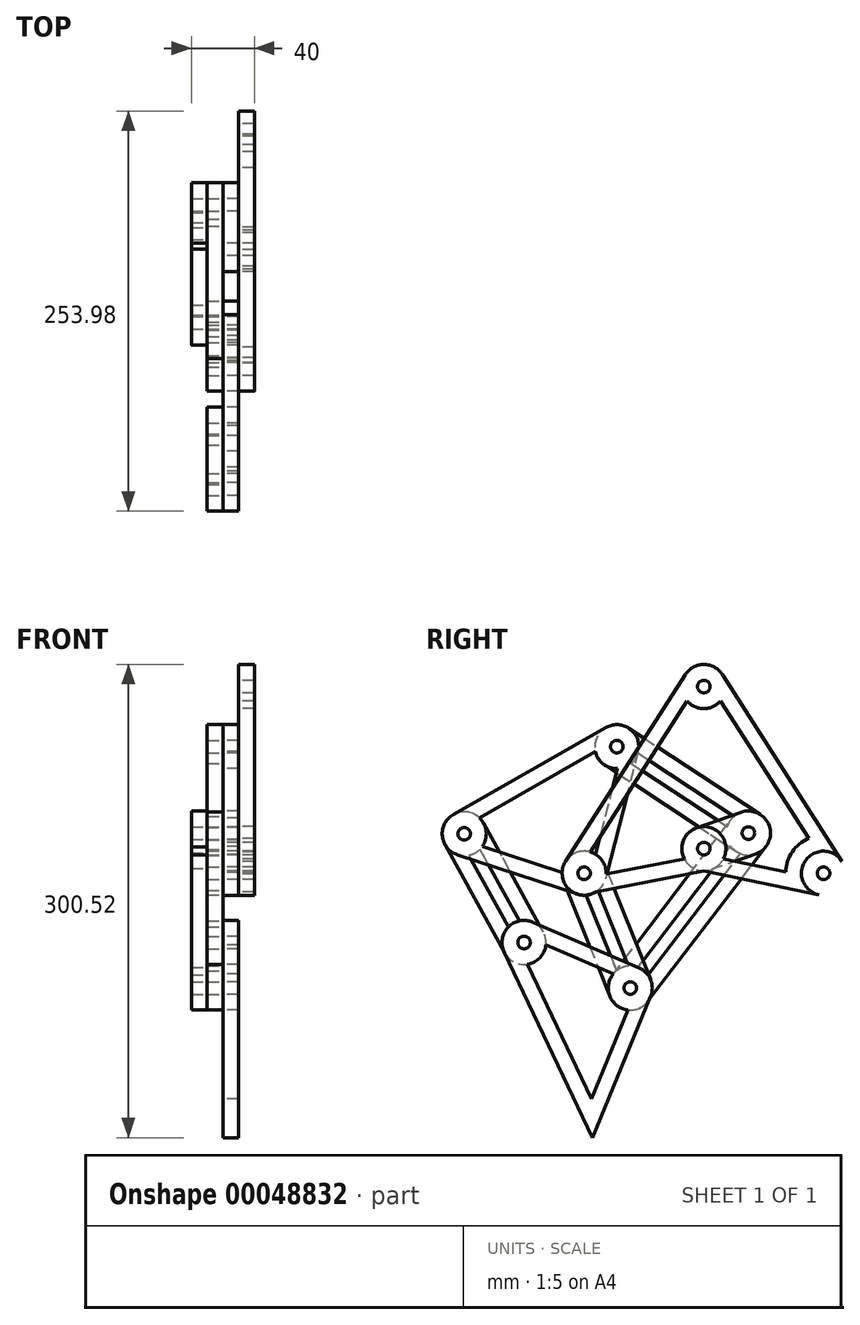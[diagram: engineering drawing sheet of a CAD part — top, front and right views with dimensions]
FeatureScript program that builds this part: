
annotation { "Feature Type Name" : "Feature", "Feature Type Description" : "" }
export const myFeature = defineFeature(function(context is Context, id is Id, definition is map)
    precondition{}
    {
        {
            assignVariable(context, id + "F0", {"name" : "WALL", "anyValue" : 10});
        }
        {
            var Q0;
            Q0=qCreatedBy(makeId("Right.planeOp"),FACE);
            var sketch = newSketch(context, id + "F1", { "sketchPlane" : qUnion([Q0])});
            skCircle(sketch, "E0", {"center": v(0, 0) * mm, "radius": 5.71 * mm});
            skLineSegment(sketch, "E1", {"start": v(0, 0) * mm, "end": v(28.32, 9.9) * mm});
            skLineSegment(sketch, "E2", {"start": v(28.32, 9.9) * mm, "end": v(-55.28, 64.77) * mm});
            skLineSegment(sketch, "E3", {"start": v(-55.28, 64.77) * mm, "end": v(-76, -15.6) * mm});
            skLineSegment(sketch, "E4", {"start": v(-76, -15.6) * mm, "end": v(-46.74, -88.55) * mm});
            skLineSegment(sketch, "E5", {"start": v(-46.74, -88.55) * mm, "end": v(28.32, 9.9) * mm});
            skLineSegment(sketch, "E6", {"start": v(-76, -15.6) * mm, "end": v(-152.2, 9.43) * mm});
            skLineSegment(sketch, "E7", {"start": v(-152.2, 9.43) * mm, "end": v(-55.28, 64.77) * mm});
            skLineSegment(sketch, "E8", {"start": v(-46.74, -88.55) * mm, "end": v(-114.19, -59.6) * mm});
            skLineSegment(sketch, "E9", {"start": v(-114.19, -59.6) * mm, "end": v(-152.2, 9.43) * mm});
            skLineSegment(sketch, "E10", {"start": v(-114.19, -59.6) * mm, "end": v(-70.68, -183.58) * mm});
            skLineSegment(sketch, "E11", {"start": v(-70.68, -183.58) * mm, "end": v(-46.74, -88.55) * mm});
            skCircle(sketch, "E12", {"center": v(-76, -15.6) * mm, "radius": 83 * mm, "construction": true});
            skLineSegment(sketch, "E13", {"start": v(0, 0) * mm, "end": v(-22.73, 19.58) * mm});
            skCircle(sketch, "E14", {"center": v(-55.28, 64.77) * mm, "radius": 14 * mm, "construction": true});
            skCircle(sketch, "E15", {"center": v(28.32, 9.9) * mm, "radius": 14 * mm, "construction": true});
            skCircle(sketch, "E16", {"center": v(0, 0) * mm, "radius": 44 * mm, "construction": true});
            skLineSegment(sketch, "E17", {"start": v(0, 0) * mm, "end": v(0, 67.08) * mm, "construction": true});
            skSolve(sketch);
        }
        {
            var Q0;
            Q0=qCreatedBy(makeId("Right.planeOp"),FACE);
            var sketch = newSketch(context, id + "F2", { "sketchPlane" : qUnion([Q0])});
            skLineSegment(sketch, "E18.rect.bottom", {"start": v(-228.6, 228.6) * mm, "end": v(228.6, 228.6) * mm, "construction": true});
            skLineSegment(sketch, "E18.rect.top", {"start": v(-228.6, -228.6) * mm, "end": v(228.6, -228.6) * mm, "construction": true});
            skLineSegment(sketch, "E18.rect.left", {"start": v(-228.6, 228.6) * mm, "end": v(-228.6, -228.6) * mm, "construction": true});
            skLineSegment(sketch, "E18.rect.right", {"start": v(228.6, 228.6) * mm, "end": v(228.6, -228.6) * mm, "construction": true});
            skPoint(sketch, "E18.rect.middle", {"position": v(0, 0) * mm});
            skSolve(sketch);
        }
        {
            var Q0;
            Q0=qCreatedBy(makeId("Right.planeOp"),FACE);
            var sketch = newSketch(context, id + "F3", { "sketchPlane" : qUnion([Q0])});
            skCircle(sketch, "E19", {"center": v(-152.2, 9.43) * mm, "radius": 4 * mm});
            skCircle(sketch, "E20", {"center": v(-55.28, 64.77) * mm, "radius": 4 * mm});
            skCircle(sketch, "E21", {"center": v(-76, -15.6) * mm, "radius": 4 * mm});
            skCircle(sketch, "E22", {"center": v(0, 0) * mm, "radius": 4 * mm});
            skCircle(sketch, "E23", {"center": v(28.32, 9.9) * mm, "radius": 4 * mm});
            skCircle(sketch, "E24", {"center": v(-114.19, -59.6) * mm, "radius": 4 * mm});
            skCircle(sketch, "E25", {"center": v(-46.74, -88.55) * mm, "radius": 4 * mm});
            skCircle(sketch, "E26", {"center": v(-152.2, 9.43) * mm, "radius": 14 * mm});
            skCircle(sketch, "E27", {"center": v(-114.19, -59.6) * mm, "radius": 14 * mm});
            skCircle(sketch, "E28", {"center": v(-46.74, -88.55) * mm, "radius": 14 * mm});
            skCircle(sketch, "E29", {"center": v(-76, -15.6) * mm, "radius": 14 * mm});
            skCircle(sketch, "E30", {"center": v(-55.28, 64.77) * mm, "radius": 14 * mm});
            skCircle(sketch, "E31", {"center": v(28.32, 9.9) * mm, "radius": 14 * mm});
            skCircle(sketch, "E32", {"center": v(0, 0) * mm, "radius": 14 * mm});
            skCircle(sketch, "E33", {"center": v(-22.73, 19.58) * mm, "radius": 4 * mm});
            skCircle(sketch, "E34", {"center": v(-22.73, 19.58) * mm, "radius": 14 * mm});
            skLineSegment(sketch, "E35", {"start": v(-159.13, 21.6) * mm, "end": v(-62.22, 76.93) * mm});
            skLineSegment(sketch, "E36", {"start": v(-41.72, 61.28) * mm, "end": v(-62.44, -19.1) * mm});
            skLineSegment(sketch, "E37", {"start": v(-80.37, -28.9) * mm, "end": v(-156.56, -3.87) * mm});
            skLineSegment(sketch, "E38", {"start": v(-108.67, -46.73) * mm, "end": v(-41.22, -75.69) * mm});
            skLineSegment(sketch, "E39", {"start": v(-126.83, -65.61) * mm, "end": v(-70.68, -183.58) * mm});
            skLineSegment(sketch, "E40", {"start": v(-70.68, -183.58) * mm, "end": v(-33.8, -93.88) * mm});
            skLineSegment(sketch, "E41", {"start": v(4.62, -13.22) * mm, "end": v(32.94, -3.32) * mm});
            skLineSegment(sketch, "E42", {"start": v(-4.62, 13.22) * mm, "end": v(23.7, 23.11) * mm});
            skSolve(sketch);
        }
        {
            var Q0;
            Q0=qCreatedBy(makeId("Right.planeOp"),FACE);
            var sketch = newSketch(context, id + "F4", { "sketchPlane" : qUnion([Q0])});
            skCircle(sketch, "E43.0", {"center": v(-152.2, 9.43) * mm, "radius": 14 * mm});
            skCircle(sketch, "E43.1", {"center": v(-76, -15.6) * mm, "radius": 14 * mm});
            skCircle(sketch, "E43.2", {"center": v(-114.19, -59.6) * mm, "radius": 14 * mm});
            skCircle(sketch, "E43.3", {"center": v(-46.74, -88.55) * mm, "radius": 14 * mm});
            skCircle(sketch, "E43.4", {"center": v(-55.28, 64.77) * mm, "radius": 14 * mm});
            skCircle(sketch, "E43.5", {"center": v(28.32, 9.9) * mm, "radius": 14 * mm});
            skLineSegment(sketch, "E44", {"start": v(-164.46, 2.68) * mm, "end": v(-126.45, -66.35) * mm});
            skLineSegment(sketch, "E45", {"start": v(-101.92, -52.84) * mm, "end": v(-139.93, 16.19) * mm});
            skLineSegment(sketch, "E46", {"start": v(-89, -20.81) * mm, "end": v(-59.74, -93.76) * mm});
            skLineSegment(sketch, "E47", {"start": v(-63, -10.39) * mm, "end": v(-33.75, -83.34) * mm});
            skLineSegment(sketch, "E48", {"start": v(-47.6, 76.48) * mm, "end": v(36, 21.6) * mm});
            skLineSegment(sketch, "E49", {"start": v(-62.96, 53.07) * mm, "end": v(20.64, -1.8) * mm});
            skCircle(sketch, "E50.0", {"center": v(-152.2, 9.43) * mm, "radius": 4 * mm});
            skCircle(sketch, "E50.1", {"center": v(-114.19, -59.6) * mm, "radius": 4 * mm});
            skCircle(sketch, "E50.2", {"center": v(-76, -15.6) * mm, "radius": 4 * mm});
            skCircle(sketch, "E50.3", {"center": v(-46.74, -88.55) * mm, "radius": 4 * mm});
            skCircle(sketch, "E50.4", {"center": v(-55.28, 64.77) * mm, "radius": 4 * mm});
            skCircle(sketch, "E50.5", {"center": v(28.32, 9.9) * mm, "radius": 4 * mm});
            skSolve(sketch);
        }
        {
            var Q0;
            Q0=qCreatedBy(makeId("Right.planeOp"),FACE);
            var sketch = newSketch(context, id + "F5", { "sketchPlane" : qUnion([Q0])});
            skCircle(sketch, "E51.0", {"center": v(-46.74, -88.55) * mm, "radius": 4 * mm});
            skCircle(sketch, "E51.1", {"center": v(-46.74, -88.55) * mm, "radius": 14 * mm});
            skCircle(sketch, "E51.2", {"center": v(28.32, 9.9) * mm, "radius": 4 * mm});
            skCircle(sketch, "E51.3", {"center": v(28.32, 9.9) * mm, "radius": 14 * mm});
            skCircle(sketch, "E51.4", {"center": v(0, 0) * mm, "radius": 4 * mm});
            skCircle(sketch, "E51.5", {"center": v(-76, -15.6) * mm, "radius": 4 * mm});
            skCircle(sketch, "E51.6", {"center": v(-76, -15.6) * mm, "radius": 14 * mm});
            skCircle(sketch, "E51.7", {"center": v(0, 0) * mm, "radius": 14 * mm});
            skLineSegment(sketch, "E52", {"start": v(-57.87, -80.06) * mm, "end": v(17.19, 18.39) * mm});
            skLineSegment(sketch, "E53", {"start": v(-35.6, -97.04) * mm, "end": v(39.45, 1.4) * mm});
            skCircle(sketch, "E54", {"center": v(0, 102.94) * mm, "radius": 4 * mm});
            skCircle(sketch, "E55", {"center": v(0, 102.94) * mm, "radius": 14 * mm});
            skLineSegment(sketch, "E56", {"start": v(-87.79, -8.04) * mm, "end": v(-11.79, 110.5) * mm});
            skCircle(sketch, "E57.MirrorC", {"center": v(76, -15.6) * mm, "radius": 4 * mm});
            skCircle(sketch, "E58.MirrorC", {"center": v(76, -15.6) * mm, "radius": 14 * mm});
            skLineSegment(sketch, "E59", {"start": v(87.79, -8.04) * mm, "end": v(11.79, 110.5) * mm});
            skLineSegment(sketch, "E60", {"start": v(-68.65, -27.51) * mm, "end": v(0, -14.26) * mm});
            skLineSegment(sketch, "E61", {"start": v(0, -14.26) * mm, "end": v(73.18, -29.31) * mm});
            skSolve(sketch);
        }
        {
            var Q0;
            Q0=makeQuery(id+"F3.imprint","IMPRINT",FACE,{"disambiguationData":[TD([[makeQuery(id+"F3.imprint","IMPRINT",EDGE,{"derivedFrom":sQuery(id+"F3.wireOp",EDGE,"E19")}),-1.0]])]});
            var Q1;
            {var subQ3=sQuery(id+"F3.wireOp",EDGE,"E35");Q1=makeQuery(id+"F3.imprint","IMPRINT",FACE,{"disambiguationData":[TD([[makeQuery(id+"F3.imprint","IMPRINT",EDGE,{"derivedFrom":subQ3}),-1.0]])]});}
            var Q2;
            Q2=makeQuery(id+"F3.imprint","IMPRINT",FACE,{"disambiguationData":[TD([[makeQuery(id+"F3.imprint","IMPRINT",EDGE,{"derivedFrom":sQuery(id+"F3.wireOp",EDGE,"E21")}),-1.0]])]});
            var Q3;
            Q3=makeQuery(id+"F3.imprint","IMPRINT",FACE,{"disambiguationData":[TD([[makeQuery(id+"F3.imprint","IMPRINT",EDGE,{"derivedFrom":sQuery(id+"F3.wireOp",EDGE,"E20")}),-1.0]])]});
            var Q4;
            Q4=makeQuery(id+"F3.imprint","IMPRINT",FACE,{"disambiguationData":[TD([[makeQuery(id+"F3.imprint","IMPRINT",EDGE,{"derivedFrom":sQuery(id+"F3.wireOp",EDGE,"E22")}),-1.0]])]});
            var Q5;
            {var subQ0=sQuery(id+"F3.wireOp",EDGE,"E41");Q5=makeQuery(id+"F3.imprint","IMPRINT",FACE,{"disambiguationData":[TD([[makeQuery(id+"F3.imprint","IMPRINT",EDGE,{"derivedFrom":subQ0}),1.0]])]});}
            var Q6;
            Q6=makeQuery(id+"F3.imprint","IMPRINT",FACE,{"disambiguationData":[TD([[makeQuery(id+"F3.imprint","IMPRINT",EDGE,{"derivedFrom":sQuery(id+"F3.wireOp",EDGE,"E23")}),-1.0]])]});
            var Q7;
            {var subQ3=sQuery(id+"F3.wireOp",EDGE,"E38");Q7=makeQuery(id+"F3.imprint","IMPRINT",FACE,{"disambiguationData":[TD([[makeQuery(id+"F3.imprint","IMPRINT",EDGE,{"derivedFrom":subQ3}),-1.0]])]});}
            var Q8;
            Q8=makeQuery(id+"F3.imprint","IMPRINT",FACE,{"disambiguationData":[TD([[makeQuery(id+"F3.imprint","IMPRINT",EDGE,{"derivedFrom":sQuery(id+"F3.wireOp",EDGE,"E24")}),-1.0]])]});
            var Q9;
            Q9=makeQuery(id+"F3.imprint","IMPRINT",FACE,{"disambiguationData":[TD([[makeQuery(id+"F3.imprint","IMPRINT",EDGE,{"derivedFrom":sQuery(id+"F3.wireOp",EDGE,"E25")}),-1.0]])]});
            extrude(context, id + "F6", {"entities" : qUnion([Q0, Q1, Q2, Q3, Q4, Q5, Q6, Q7, Q8, Q9]), "depth" : (getVariable(context, 'WALL')) * mm});
        }
        {
            var Q0;
            Q0=makeQuery(id+"F4.imprint","IMPRINT",FACE,{"disambiguationData":[TD([[makeQuery(id+"F4.imprint","IMPRINT",EDGE,{"derivedFrom":sQuery(id+"F4.wireOp",EDGE,"E50.0")}),-1.0]])]});
            var Q1;
            {var subQ1=sQuery(id+"F4.wireOp",EDGE,"E44");Q1=makeQuery(id+"F4.imprint","IMPRINT",FACE,{"disambiguationData":[TD([[makeQuery(id+"F4.imprint","IMPRINT",EDGE,{"derivedFrom":subQ1}),1.0]])]});}
            var Q2;
            Q2=makeQuery(id+"F4.imprint","IMPRINT",FACE,{"disambiguationData":[TD([[makeQuery(id+"F4.imprint","IMPRINT",EDGE,{"derivedFrom":sQuery(id+"F4.wireOp",EDGE,"E50.1")}),-1.0]])]});
            var Q3;
            Q3=makeQuery(id+"F4.imprint","IMPRINT",FACE,{"disambiguationData":[TD([[makeQuery(id+"F4.imprint","IMPRINT",EDGE,{"derivedFrom":sQuery(id+"F4.wireOp",EDGE,"E50.2")}),-1.0]])]});
            var Q4;
            {var subQ1=sQuery(id+"F4.wireOp",EDGE,"E46");Q4=makeQuery(id+"F4.imprint","IMPRINT",FACE,{"disambiguationData":[TD([[makeQuery(id+"F4.imprint","IMPRINT",EDGE,{"derivedFrom":subQ1}),1.0]])]});}
            var Q5;
            Q5=makeQuery(id+"F4.imprint","IMPRINT",FACE,{"disambiguationData":[TD([[makeQuery(id+"F4.imprint","IMPRINT",EDGE,{"derivedFrom":sQuery(id+"F4.wireOp",EDGE,"E50.3")}),-1.0]])]});
            var Q6;
            Q6=makeQuery(id+"F4.imprint","IMPRINT",FACE,{"disambiguationData":[TD([[makeQuery(id+"F4.imprint","IMPRINT",EDGE,{"derivedFrom":sQuery(id+"F4.wireOp",EDGE,"E50.4")}),-1.0]])]});
            var Q7;
            {var subQ1=sQuery(id+"F4.wireOp",EDGE,"E48");Q7=makeQuery(id+"F4.imprint","IMPRINT",FACE,{"disambiguationData":[TD([[makeQuery(id+"F4.imprint","IMPRINT",EDGE,{"derivedFrom":subQ1}),-1.0]])]});}
            var Q8;
            Q8=makeQuery(id+"F4.imprint","IMPRINT",FACE,{"disambiguationData":[TD([[makeQuery(id+"F4.imprint","IMPRINT",EDGE,{"derivedFrom":sQuery(id+"F4.wireOp",EDGE,"E50.5")}),-1.0]])]});
            extrude(context, id + "F7", {"entities" : qUnion([Q0, Q1, Q2, Q3, Q4, Q5, Q6, Q7, Q8]), "oppositeDirection" : true, "depth" : (getVariable(context, 'WALL')) * mm});
        }
        {
            var Q0;
            Q0=makeQuery(id+"F5.imprint","IMPRINT",FACE,{"disambiguationData":[TD([[makeQuery(id+"F5.imprint","IMPRINT",EDGE,{"derivedFrom":sQuery(id+"F5.wireOp",EDGE,"E51.2")}),-1.0]])]});
            var Q1;
            {var subQ3=sQuery(id+"F5.wireOp",EDGE,"E51.3");var subQ5=sQuery(id+"F5.wireOp",EDGE,"E52");var subQ6=makeQuery(id+"F5.imprint","INTERSECT",VERTEX,{"derivedFrom":[subQ3,subQ5]});Q1=makeQuery(id+"F5.imprint","IMPRINT",FACE,{"disambiguationData":[TD([[makeQuery(id+"F5.imprint","IMPRINT",EDGE,{"disambiguationData":[TD([[subQ6,-1.0]])],"derivedFrom":subQ3}),-1.0]])]});}
            var Q2;
            {var subQ0=sQuery(id+"F5.wireOp",EDGE,"E52");var subQ1=sQuery(id+"F5.wireOp",EDGE,"E51.7");var subQ3=makeQuery(id+"F5.imprint","INTERSECT",VERTEX,{"disambiguationData":[OD(0.0)],"derivedFrom":[subQ1,subQ0]});Q2=makeQuery(id+"F5.imprint","IMPRINT",FACE,{"disambiguationData":[TD([[makeQuery(id+"F5.imprint","IMPRINT",EDGE,{"disambiguationData":[TD([[subQ3,-1.0]])],"derivedFrom":subQ1}),1.0]])]});}
            var Q3;
            {var subQ3=sQuery(id+"F5.wireOp",EDGE,"E52");var subQ5=sQuery(id+"F5.wireOp",EDGE,"E51.1");var subQ7=makeQuery(id+"F5.imprint","INTERSECT",VERTEX,{"derivedFrom":[subQ5,subQ3]});Q3=makeQuery(id+"F5.imprint","IMPRINT",FACE,{"disambiguationData":[TD([[makeQuery(id+"F5.imprint","IMPRINT",EDGE,{"disambiguationData":[TD([[subQ7,1.0]])],"derivedFrom":subQ5}),-1.0]])]});}
            var Q4;
            Q4=makeQuery(id+"F5.imprint","IMPRINT",FACE,{"disambiguationData":[TD([[makeQuery(id+"F5.imprint","IMPRINT",EDGE,{"derivedFrom":sQuery(id+"F5.wireOp",EDGE,"E51.0")}),-1.0]])]});
            extrude(context, id + "F8", {"entities" : qUnion([Q0, Q1, Q2, Q3, Q4]), "oppositeDirection" : true, "depth" : (getVariable(context, 'WALL') * 2) * mm, "hasSecondDirection" : true, "secondDirectionOppositeDirection" : true, "secondDirectionDepth" : (getVariable(context, 'WALL')) * mm});
        }
        {
            var Q0;
            Q0=makeQuery(id+"F5.imprint","IMPRINT",FACE,{"disambiguationData":[TD([[makeQuery(id+"F5.imprint","IMPRINT",EDGE,{"derivedFrom":sQuery(id+"F5.wireOp",EDGE,"E51.5")}),-1.0]])]});
            var Q1;
            {var subQ15=sQuery(id+"F5.wireOp",EDGE,"E56");Q1=makeQuery(id+"F5.imprint","IMPRINT",FACE,{"disambiguationData":[TD([[makeQuery(id+"F5.imprint","IMPRINT",EDGE,{"derivedFrom":subQ15}),-1.0]])]});}
            var Q2;
            Q2=makeQuery(id+"F5.imprint","IMPRINT",FACE,{"disambiguationData":[TD([[makeQuery(id+"F5.imprint","IMPRINT",EDGE,{"derivedFrom":sQuery(id+"F5.wireOp",EDGE,"E54")}),-1.0]])]});
            var Q3;
            Q3=makeQuery(id+"F5.imprint","IMPRINT",FACE,{"disambiguationData":[TD([[makeQuery(id+"F5.imprint","IMPRINT",EDGE,{"derivedFrom":sQuery(id+"F5.wireOp",EDGE,"E51.4")}),-1.0]])]});
            var Q4;
            {var subQ0=sQuery(id+"F5.wireOp",EDGE,"E52");var subQ1=sQuery(id+"F5.wireOp",EDGE,"E51.7");var subQ3=makeQuery(id+"F5.imprint","INTERSECT",VERTEX,{"disambiguationData":[OD(0.0)],"derivedFrom":[subQ1,subQ0]});Q4=makeQuery(id+"F5.imprint","IMPRINT",FACE,{"disambiguationData":[TD([[makeQuery(id+"F5.imprint","IMPRINT",EDGE,{"disambiguationData":[TD([[subQ3,-1.0]])],"derivedFrom":subQ1}),1.0]])]});}
            var Q5;
            {var subQ3=sQuery(id+"F5.wireOp",EDGE,"E51.3");var subQ5=sQuery(id+"F5.wireOp",EDGE,"E52");var subQ6=makeQuery(id+"F5.imprint","INTERSECT",VERTEX,{"derivedFrom":[subQ3,subQ5]});Q5=makeQuery(id+"F5.imprint","IMPRINT",FACE,{"disambiguationData":[TD([[makeQuery(id+"F5.imprint","IMPRINT",EDGE,{"disambiguationData":[TD([[subQ6,-1.0]])],"derivedFrom":subQ3}),-1.0]])]});}
            var Q6;
            Q6=makeQuery(id+"F5.imprint","IMPRINT",FACE,{"disambiguationData":[TD([[makeQuery(id+"F5.imprint","IMPRINT",EDGE,{"derivedFrom":sQuery(id+"F5.wireOp",EDGE,"E51.2")}),-1.0]])]});
            var Q7;
            Q7=makeQuery(id+"F5.imprint","IMPRINT",FACE,{"disambiguationData":[TD([[makeQuery(id+"F5.imprint","IMPRINT",EDGE,{"derivedFrom":sQuery(id+"F5.wireOp",EDGE,"E51.2")}),1.0]])]});
            var Q8;
            Q8=makeQuery(id+"F5.imprint","IMPRINT",FACE,{"disambiguationData":[TD([[makeQuery(id+"F5.imprint","IMPRINT",EDGE,{"derivedFrom":sQuery(id+"F5.wireOp",EDGE,"E57.MirrorC")}),1.0]])]});
            extrude(context, id + "F9", {"entities" : qUnion([Q0, Q1, Q2, Q3, Q4, Q5, Q6, Q7, Q8]), "depth" : (getVariable(context, 'WALL') * 2) * mm, "hasSecondDirection" : true, "secondDirectionOppositeDirection" : false, "secondDirectionDepth" : (getVariable(context, 'WALL') * 1) * mm});
        }
        {
            var Q0;
            Q0=makeQuery(id+"F6.opExtrude","CAP_FACE",FACE,{"disambiguationData":[OSD([sQuery(id+"F3.wireOp",EDGE,"E19"),sQuery(id+"F3.wireOp",EDGE,"E20"),sQuery(id+"F3.wireOp",EDGE,"E21"),sQuery(id+"F3.wireOp",EDGE,"E26"),sQuery(id+"F3.wireOp",EDGE,"E29"),sQuery(id+"F3.wireOp",EDGE,"E30"),sQuery(id+"F3.wireOp",EDGE,"E35"),sQuery(id+"F3.wireOp",EDGE,"E36"),sQuery(id+"F3.wireOp",EDGE,"E37")])],"isStart":false});
            var Q1;
            Q1=makeQuery(id+"F6.opExtrude","CAP_FACE",FACE,{"disambiguationData":[OSD([sQuery(id+"F3.wireOp",EDGE,"E19"),sQuery(id+"F3.wireOp",EDGE,"E20"),sQuery(id+"F3.wireOp",EDGE,"E21"),sQuery(id+"F3.wireOp",EDGE,"E26"),sQuery(id+"F3.wireOp",EDGE,"E29"),sQuery(id+"F3.wireOp",EDGE,"E30"),sQuery(id+"F3.wireOp",EDGE,"E35"),sQuery(id+"F3.wireOp",EDGE,"E36"),sQuery(id+"F3.wireOp",EDGE,"E37")])],"isStart":true});
            var Q2;
            Q2=makeQuery(id+"F6.opExtrude","CAP_FACE",FACE,{"disambiguationData":[OSD([sQuery(id+"F3.wireOp",EDGE,"E24"),sQuery(id+"F3.wireOp",EDGE,"E25"),sQuery(id+"F3.wireOp",EDGE,"E27"),sQuery(id+"F3.wireOp",EDGE,"E28"),sQuery(id+"F3.wireOp",EDGE,"E38"),sQuery(id+"F3.wireOp",EDGE,"E39"),sQuery(id+"F3.wireOp",EDGE,"E40")])],"isStart":false});
            var Q3;
            Q3=makeQuery(id+"F6.opExtrude","CAP_FACE",FACE,{"disambiguationData":[OSD([sQuery(id+"F3.wireOp",EDGE,"E24"),sQuery(id+"F3.wireOp",EDGE,"E25"),sQuery(id+"F3.wireOp",EDGE,"E27"),sQuery(id+"F3.wireOp",EDGE,"E28"),sQuery(id+"F3.wireOp",EDGE,"E38"),sQuery(id+"F3.wireOp",EDGE,"E39"),sQuery(id+"F3.wireOp",EDGE,"E40")])],"isStart":true});
            var Q4;
            Q4=makeQuery(id+"F9.opExtrude","CAP_FACE",FACE,{"disambiguationData":[OSD([sQuery(id+"F5.wireOp",EDGE,"E51.4"),sQuery(id+"F5.wireOp",EDGE,"E51.5"),sQuery(id+"F5.wireOp",EDGE,"E51.6"),sQuery(id+"F5.wireOp",EDGE,"E54"),sQuery(id+"F5.wireOp",EDGE,"E55"),sQuery(id+"F5.wireOp",EDGE,"E56"),sQuery(id+"F5.wireOp",EDGE,"E57.MirrorC"),sQuery(id+"F5.wireOp",EDGE,"E58.MirrorC"),sQuery(id+"F5.wireOp",EDGE,"E59"),sQuery(id+"F5.wireOp",EDGE,"E60"),sQuery(id+"F5.wireOp",EDGE,"E61")])],"isStart":true});
            var Q5;
            Q5=makeQuery(id+"F7.opExtrude","CAP_FACE",FACE,{"disambiguationData":[OSD([sQuery(id+"F4.wireOp",EDGE,"E43.0"),sQuery(id+"F4.wireOp",EDGE,"E43.2"),sQuery(id+"F4.wireOp",EDGE,"E44"),sQuery(id+"F4.wireOp",EDGE,"E45"),sQuery(id+"F4.wireOp",EDGE,"E50.0"),sQuery(id+"F4.wireOp",EDGE,"E50.1")])],"isStart":true});
            var Q6;
            Q6=makeQuery(id+"F7.opExtrude","CAP_FACE",FACE,{"disambiguationData":[OSD([sQuery(id+"F4.wireOp",EDGE,"E43.0"),sQuery(id+"F4.wireOp",EDGE,"E43.2"),sQuery(id+"F4.wireOp",EDGE,"E44"),sQuery(id+"F4.wireOp",EDGE,"E45"),sQuery(id+"F4.wireOp",EDGE,"E50.0"),sQuery(id+"F4.wireOp",EDGE,"E50.1")])],"isStart":false});
            var Q7;
            Q7=makeQuery(id+"F7.opExtrude","CAP_FACE",FACE,{"disambiguationData":[OSD([sQuery(id+"F4.wireOp",EDGE,"E43.1"),sQuery(id+"F4.wireOp",EDGE,"E43.3"),sQuery(id+"F4.wireOp",EDGE,"E46"),sQuery(id+"F4.wireOp",EDGE,"E47"),sQuery(id+"F4.wireOp",EDGE,"E50.2"),sQuery(id+"F4.wireOp",EDGE,"E50.3")])],"isStart":true});
            var Q8;
            Q8=makeQuery(id+"F7.opExtrude","CAP_FACE",FACE,{"disambiguationData":[OSD([sQuery(id+"F4.wireOp",EDGE,"E43.1"),sQuery(id+"F4.wireOp",EDGE,"E43.3"),sQuery(id+"F4.wireOp",EDGE,"E46"),sQuery(id+"F4.wireOp",EDGE,"E47"),sQuery(id+"F4.wireOp",EDGE,"E50.2"),sQuery(id+"F4.wireOp",EDGE,"E50.3")])],"isStart":false});
            var Q9;
            Q9=makeQuery(id+"F8.opExtrude","CAP_FACE",FACE,{"disambiguationData":[OSD([sQuery(id+"F5.wireOp",EDGE,"E51.0"),sQuery(id+"F5.wireOp",EDGE,"E51.1"),sQuery(id+"F5.wireOp",EDGE,"E51.2"),sQuery(id+"F5.wireOp",EDGE,"E51.3"),sQuery(id+"F5.wireOp",EDGE,"E52"),sQuery(id+"F5.wireOp",EDGE,"E53")])],"isStart":false});
            var Q10;
            Q10=makeQuery(id+"F7.opExtrude","CAP_FACE",FACE,{"disambiguationData":[OSD([sQuery(id+"F4.wireOp",EDGE,"E43.4"),sQuery(id+"F4.wireOp",EDGE,"E43.5"),sQuery(id+"F4.wireOp",EDGE,"E48"),sQuery(id+"F4.wireOp",EDGE,"E49"),sQuery(id+"F4.wireOp",EDGE,"E50.4"),sQuery(id+"F4.wireOp",EDGE,"E50.5")])],"isStart":false});
            var Q11;
            Q11=makeQuery(id+"F8.opExtrude","CAP_FACE",FACE,{"disambiguationData":[OSD([sQuery(id+"F5.wireOp",EDGE,"E51.0"),sQuery(id+"F5.wireOp",EDGE,"E51.1"),sQuery(id+"F5.wireOp",EDGE,"E51.2"),sQuery(id+"F5.wireOp",EDGE,"E51.3"),sQuery(id+"F5.wireOp",EDGE,"E52"),sQuery(id+"F5.wireOp",EDGE,"E53")])],"isStart":true});
            var Q12;
            Q12=makeQuery(id+"F7.opExtrude","CAP_FACE",FACE,{"disambiguationData":[OSD([sQuery(id+"F4.wireOp",EDGE,"E43.4"),sQuery(id+"F4.wireOp",EDGE,"E43.5"),sQuery(id+"F4.wireOp",EDGE,"E48"),sQuery(id+"F4.wireOp",EDGE,"E49"),sQuery(id+"F4.wireOp",EDGE,"E50.4"),sQuery(id+"F4.wireOp",EDGE,"E50.5")])],"isStart":true});
            var Q13;
            Q13=makeQuery(id+"F9.opExtrude","CAP_FACE",FACE,{"disambiguationData":[OSD([sQuery(id+"F5.wireOp",EDGE,"E51.4"),sQuery(id+"F5.wireOp",EDGE,"E51.5"),sQuery(id+"F5.wireOp",EDGE,"E51.6"),sQuery(id+"F5.wireOp",EDGE,"E54"),sQuery(id+"F5.wireOp",EDGE,"E55"),sQuery(id+"F5.wireOp",EDGE,"E56"),sQuery(id+"F5.wireOp",EDGE,"E57.MirrorC"),sQuery(id+"F5.wireOp",EDGE,"E58.MirrorC"),sQuery(id+"F5.wireOp",EDGE,"E59"),sQuery(id+"F5.wireOp",EDGE,"E60"),sQuery(id+"F5.wireOp",EDGE,"E61")])],"isStart":false});
            shell(context, id + "F10", {"entities" : qUnion([Q0, Q1, Q2, Q3, Q4, Q5, Q6, Q7, Q8, Q9, Q10, Q11, Q12, Q13]), "thickness" : (getVariable(context, 'WALL')) * mm});
        }
    });
